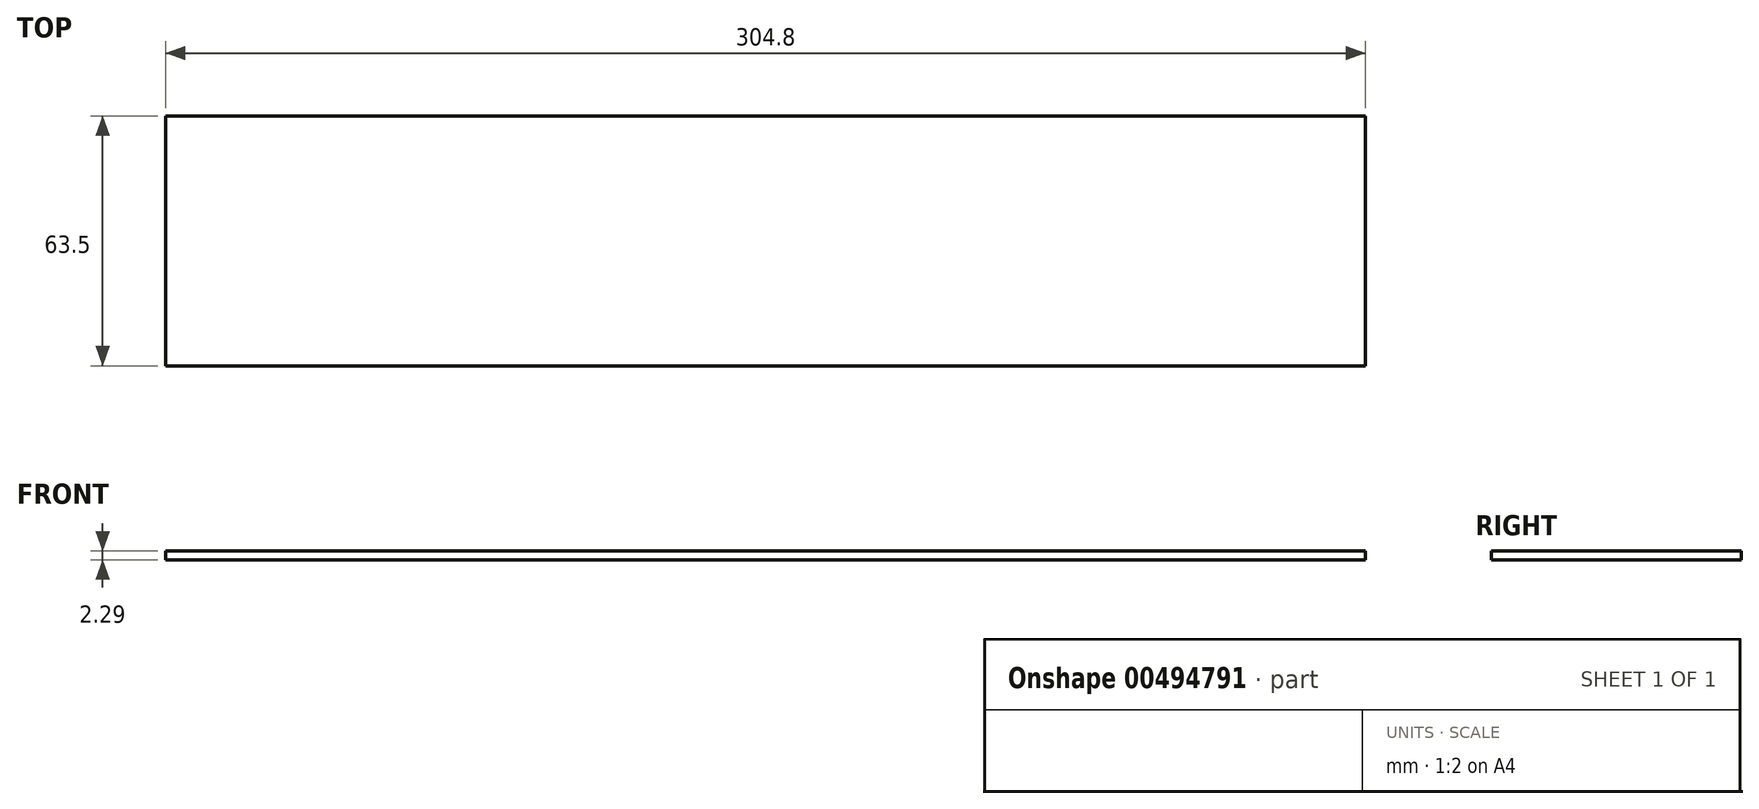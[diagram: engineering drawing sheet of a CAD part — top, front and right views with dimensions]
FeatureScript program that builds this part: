
annotation { "Feature Type Name" : "Feature", "Feature Type Description" : "" }
export const myFeature = defineFeature(function(context is Context, id is Id, definition is map)
    precondition{}
    {
        {
            var Q0;
            Q0=qCreatedBy(makeId("Top.planeOp"),FACE);
            var sketch = newSketch(context, id + "F0", { "sketchPlane" : qUnion([Q0])});
            skLineSegment(sketch, "E0.bottom", {"start": v(152.4, 31.75) * mm, "end": v(-152.4, 31.75) * mm});
            skLineSegment(sketch, "E0.top", {"start": v(152.4, -31.75) * mm, "end": v(-152.4, -31.75) * mm});
            skLineSegment(sketch, "E0.left", {"start": v(152.4, 31.75) * mm, "end": v(152.4, -31.75) * mm});
            skLineSegment(sketch, "E0.right", {"start": v(-152.4, 31.75) * mm, "end": v(-152.4, -31.75) * mm});
            skPoint(sketch, "E0.middle", {"position": v(0, 0) * mm});
            skSolve(sketch);
        }
        {
            var Q0;
            Q0=makeQuery(id+"F0.imprint","IMPRINT",FACE,{"disambiguationData":[TD([[makeQuery(id+"F0.imprint","IMPRINT",EDGE,{"derivedFrom":sQuery(id+"F0.wireOp",EDGE,"E0.bottom")}),1.0]])]});
            extrude(context, id + "F1", {"entities" : qUnion([Q0]), "depth" : 2.3 * mm});
        }
    });
